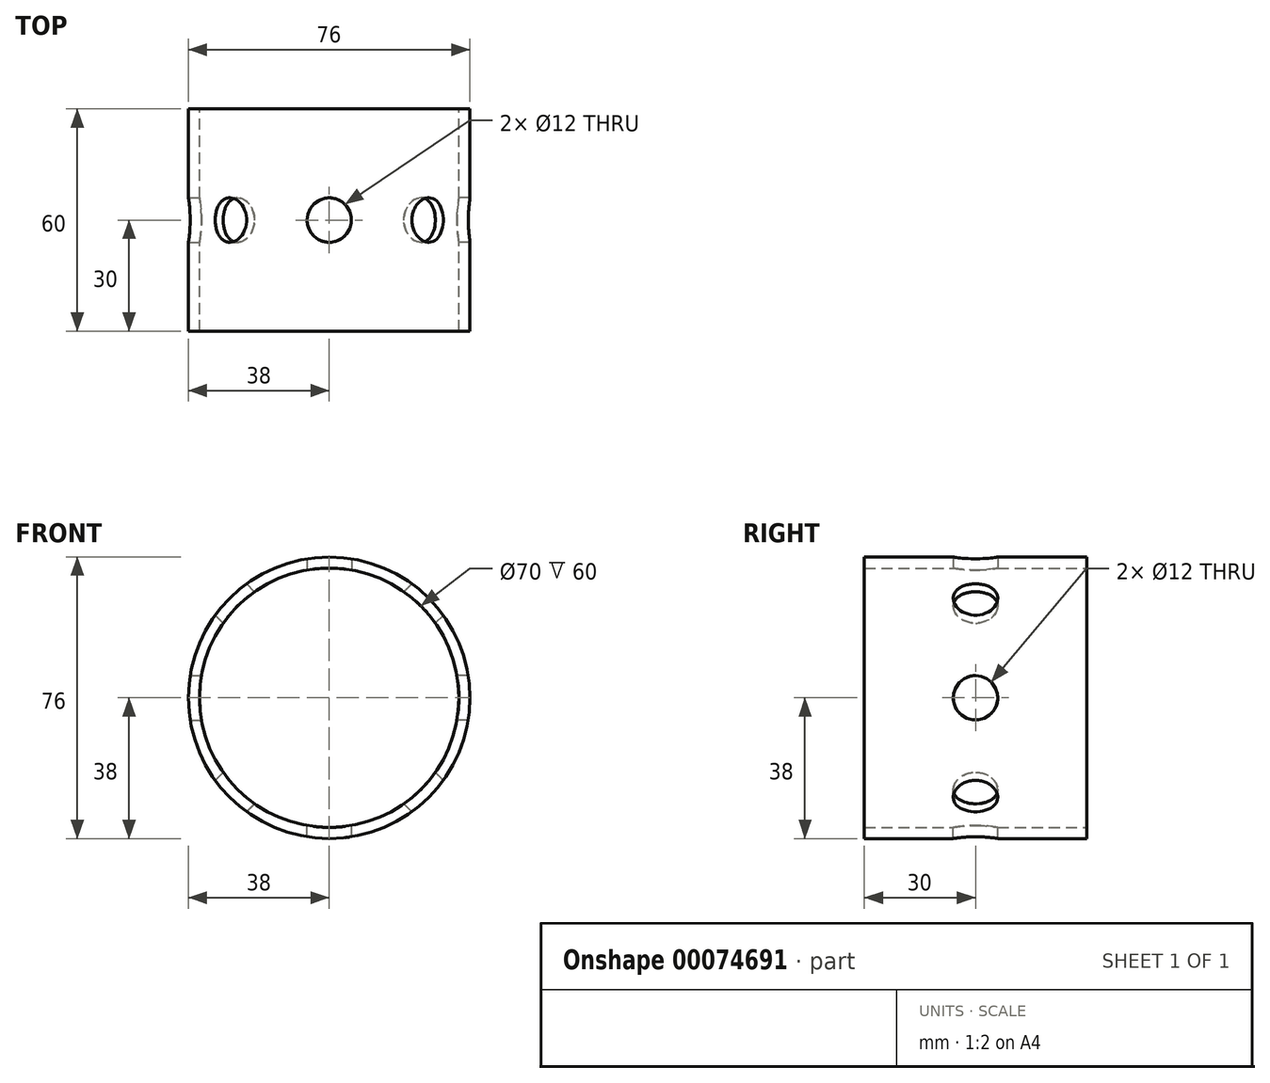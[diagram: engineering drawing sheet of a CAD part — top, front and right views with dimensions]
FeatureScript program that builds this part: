
annotation { "Feature Type Name" : "Feature", "Feature Type Description" : "" }
export const myFeature = defineFeature(function(context is Context, id is Id, definition is map)
    precondition{}
    {
        {
            var Q0;
            Q0=qCreatedBy(makeId("Front.planeOp"),FACE);
            var sketch = newSketch(context, id + "F0", { "sketchPlane" : qUnion([Q0])});
            skCircle(sketch, "E0", {"center": v(0, 0) * mm, "radius": 35 * mm});
            skCircle(sketch, "E1", {"center": v(0, 0) * mm, "radius": 38 * mm});
            skSolve(sketch);
        }
        {
            var Q0;
            Q0=makeQuery(id+"F0.imprint","IMPRINT",FACE,{"disambiguationData":[TD([[makeQuery(id+"F0.imprint","IMPRINT",EDGE,{"derivedFrom":sQuery(id+"F0.wireOp",EDGE,"E0")}),-1.0]])]});
            extrude(context, id + "F1", {"entities" : qUnion([Q0]), "depth" : 60 * mm});
        }
        {
            var Q0;
            Q0=qCreatedBy(makeId("Right.planeOp"),FACE);
            var sketch = newSketch(context, id + "F2", { "sketchPlane" : qUnion([Q0])});
            skCircle(sketch, "E2", {"center": v(-30, 0) * mm, "radius": 6 * mm});
            skSolve(sketch);
        }
        {
            var Q0;
            Q0=qCreatedBy(makeId("Right.planeOp"),FACE);
            var sketch = newSketch(context, id + "F3", { "sketchPlane" : qUnion([Q0])});
            skLineSegment(sketch, "E3", {"start": v(-72.14, 0) * mm, "end": v(0, 0) * mm, "construction": true});
            skSolve(sketch);
        }
        {
            var Q0;
            Q0=makeQuery(id+"F2.imprint","IMPRINT",FACE,{"disambiguationData":[TD([[makeQuery(id+"F2.imprint","IMPRINT",EDGE,{"derivedFrom":sQuery(id+"F2.wireOp",EDGE,"E2")}),1.0]])]});
            extrude(context, id + "F4", {"entities" : qUnion([Q0]), "operationType" : NewBodyOperationType.REMOVE, "oppositeDirection" : true, "depth" : 50 * mm});
        }
        {
            var Q0;
            Q0=makeQuery(id+"F1.opExtrude","SWEPT_BODY",BODY,{"disambiguationData":[OSD([sQuery(id+"F0.wireOp",EDGE,"E0"),sQuery(id+"F0.wireOp",EDGE,"E1")])]});
            var Q1;
            Q1=makeQuery(id+"F4.boolean.opBoolean","COPY",FACE,{"derivedFrom":makeQuery(id+"F4.opExtrude","SWEPT_FACE",FACE,{"disambiguationData":[OSD([sQuery(id+"F2.wireOp",EDGE,"E2")])]})});
            var Q2;
            Q2=sQuery(id+"F3.wireOp",EDGE,"E3");
            circularPattern(context, id + "F5", {"faces" : qUnion([Q1]), "axis" : qUnion([Q2]), "angle" : 45 * degree, "instanceCount" : 360 / 45, "patternType" : PatternType.FACE});
        }
    });
